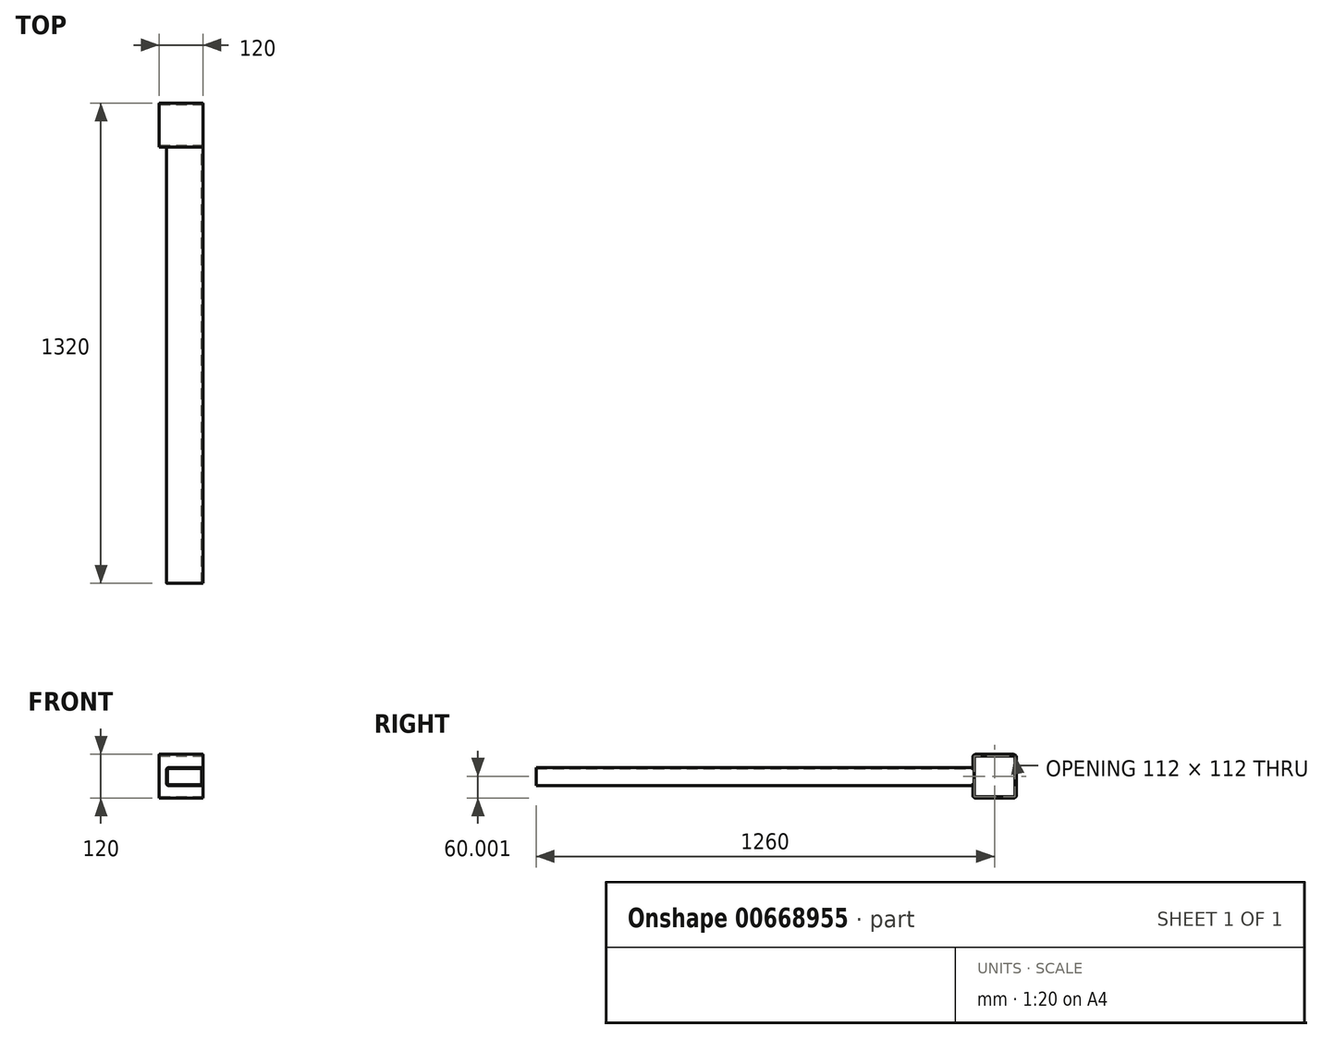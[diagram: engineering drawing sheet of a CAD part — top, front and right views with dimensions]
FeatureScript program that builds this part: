
annotation { "Feature Type Name" : "Feature", "Feature Type Description" : "" }
export const myFeature = defineFeature(function(context is Context, id is Id, definition is map)
    precondition{}
    {
        {
            var Q0;
            Q0=qCreatedBy(makeId("Front.planeOp"),FACE);
            var sketch = newSketch(context, id + "F0", { "sketchPlane" : qUnion([Q0])});
            skLineSegment(sketch, "E0.bottom", {"start": v(-29.26, 16.06) * mm, "end": v(58.74, 16.06) * mm});
            skLineSegment(sketch, "E0.top", {"start": v(-29.26, -27.94) * mm, "end": v(58.74, -27.94) * mm});
            skLineSegment(sketch, "E0.left", {"start": v(-32.26, 13.06) * mm, "end": v(-32.26, -24.94) * mm});
            skLineSegment(sketch, "E0.right", {"start": v(61.74, 13.06) * mm, "end": v(61.74, -24.94) * mm});
            skLineSegment(sketch, "E1.bottom", {"start": v(-29.26, 19.06) * mm, "end": v(58.74, 19.06) * mm});
            skLineSegment(sketch, "E1.top", {"start": v(-29.26, -30.94) * mm, "end": v(58.74, -30.94) * mm});
            skLineSegment(sketch, "E1.left", {"start": v(-35.26, 13.06) * mm, "end": v(-35.26, -24.94) * mm});
            skLineSegment(sketch, "E1.right", {"start": v(64.74, 13.06) * mm, "end": v(64.74, -24.94) * mm});
            skPoint(sketch, "E2.visualSharp", {"position": v(-32.26, 16.06) * mm});
            skArc(sketch, "E2.filletArc", {"start": v(-29.26, 16.06) * mm, "mid": v(-31.38, 15.18) * mm, "end": v(-32.26, 13.06) * mm});
            skPoint(sketch, "E3.visualSharp", {"position": v(61.74, 16.06) * mm});
            skArc(sketch, "E3.filletArc", {"start": v(61.74, 13.06) * mm, "mid": v(60.87, 15.18) * mm, "end": v(58.74, 16.06) * mm});
            skPoint(sketch, "E4.visualSharp", {"position": v(61.74, -27.94) * mm});
            skArc(sketch, "E4.filletArc", {"start": v(58.74, -27.94) * mm, "mid": v(60.87, -27.06) * mm, "end": v(61.74, -24.94) * mm});
            skPoint(sketch, "E5.visualSharp", {"position": v(-32.26, -27.94) * mm});
            skArc(sketch, "E5.filletArc", {"start": v(-32.26, -24.94) * mm, "mid": v(-31.38, -27.06) * mm, "end": v(-29.26, -27.94) * mm});
            skPoint(sketch, "E6.visualSharp", {"position": v(64.74, 19.06) * mm});
            skArc(sketch, "E6.filletArc", {"start": v(64.74, 13.06) * mm, "mid": v(62.99, 17.3) * mm, "end": v(58.74, 19.06) * mm});
            skPoint(sketch, "E7.visualSharp", {"position": v(64.74, -30.94) * mm});
            skArc(sketch, "E7.filletArc", {"start": v(58.74, -30.94) * mm, "mid": v(62.99, -29.18) * mm, "end": v(64.74, -24.94) * mm});
            skPoint(sketch, "E8.visualSharp", {"position": v(-35.26, -30.94) * mm});
            skArc(sketch, "E8.filletArc", {"start": v(-35.26, -24.94) * mm, "mid": v(-33.5, -29.18) * mm, "end": v(-29.26, -30.94) * mm});
            skPoint(sketch, "E9.visualSharp", {"position": v(-35.26, 19.06) * mm});
            skArc(sketch, "E9.filletArc", {"start": v(-29.26, 19.06) * mm, "mid": v(-33.5, 17.3) * mm, "end": v(-35.26, 13.06) * mm});
            skSolve(sketch);
        }
        {
            var Q0;
            Q0 = qSketchRegion(id + "F0", true);
            extrude(context, id + "F1", {"entities" : qUnion([Q0]), "depth" : 1200 * mm, "offsetDistance" : 25 * mm});
        }
        {
            var Q0;
            Q0=makeQuery(id+"F1.opExtrude","SWEPT_FACE",FACE,{"disambiguationData":[OSD([sQuery(id+"F0.wireOp",EDGE,"E1.right")])]});
            var sketch = newSketch(context, id + "F2", { "sketchPlane" : qUnion([Q0])});
            skLineSegment(sketch, "E10.bottom", {"start": v(8, 55.06) * mm, "end": v(112, 55.06) * mm});
            skLineSegment(sketch, "E10.top", {"start": v(8, -64.94) * mm, "end": v(112, -64.94) * mm});
            skLineSegment(sketch, "E10.left", {"start": v(0, 47.06) * mm, "end": v(0, -56.94) * mm});
            skLineSegment(sketch, "E10.right", {"start": v(120, 47.06) * mm, "end": v(120, -56.94) * mm});
            skLineSegment(sketch, "E11.bottom", {"start": v(8, 51.06) * mm, "end": v(112, 51.06) * mm});
            skLineSegment(sketch, "E11.top", {"start": v(8, -60.94) * mm, "end": v(112, -60.94) * mm});
            skLineSegment(sketch, "E11.left", {"start": v(4, 47.06) * mm, "end": v(4, -56.94) * mm});
            skLineSegment(sketch, "E11.right", {"start": v(116, 47.06) * mm, "end": v(116, -56.94) * mm});
            skPoint(sketch, "E12.visualSharp", {"position": v(4, 51.06) * mm});
            skArc(sketch, "E12.filletArc", {"start": v(8, 51.06) * mm, "mid": v(5.17, 49.89) * mm, "end": v(4, 47.06) * mm});
            skPoint(sketch, "E13.visualSharp", {"position": v(4, -60.94) * mm});
            skArc(sketch, "E13.filletArc", {"start": v(4, -56.94) * mm, "mid": v(5.17, -59.77) * mm, "end": v(8, -60.94) * mm});
            skPoint(sketch, "E14.visualSharp", {"position": v(116, -60.94) * mm});
            skArc(sketch, "E14.filletArc", {"start": v(112, -60.94) * mm, "mid": v(114.83, -59.77) * mm, "end": v(116, -56.94) * mm});
            skPoint(sketch, "E15.visualSharp", {"position": v(116, 51.06) * mm});
            skArc(sketch, "E15.filletArc", {"start": v(116, 47.06) * mm, "mid": v(114.83, 49.89) * mm, "end": v(112, 51.06) * mm});
            skPoint(sketch, "E16.visualSharp", {"position": v(120, 55.06) * mm});
            skArc(sketch, "E16.filletArc", {"start": v(120, 47.06) * mm, "mid": v(117.66, 52.72) * mm, "end": v(112, 55.06) * mm});
            skPoint(sketch, "E17.visualSharp", {"position": v(0, 55.06) * mm});
            skArc(sketch, "E17.filletArc", {"start": v(8, 55.06) * mm, "mid": v(2.34, 52.72) * mm, "end": v(0, 47.06) * mm});
            skPoint(sketch, "E18.visualSharp", {"position": v(0, -64.94) * mm});
            skArc(sketch, "E18.filletArc", {"start": v(0, -56.94) * mm, "mid": v(2.34, -62.6) * mm, "end": v(8, -64.94) * mm});
            skPoint(sketch, "E19.visualSharp", {"position": v(120, -64.94) * mm});
            skArc(sketch, "E19.filletArc", {"start": v(112, -64.94) * mm, "mid": v(117.66, -62.6) * mm, "end": v(120, -56.94) * mm});
            skSolve(sketch);
        }
        {
            var Q0;
            Q0 = qSketchRegion(id + "F2", true);
            extrude(context, id + "F3", {"entities" : qUnion([Q0]), "operationType" : NewBodyOperationType.ADD, "oppositeDirection" : true, "depth" : 120 * mm, "offsetDistance" : 25 * mm});
        }
    });
